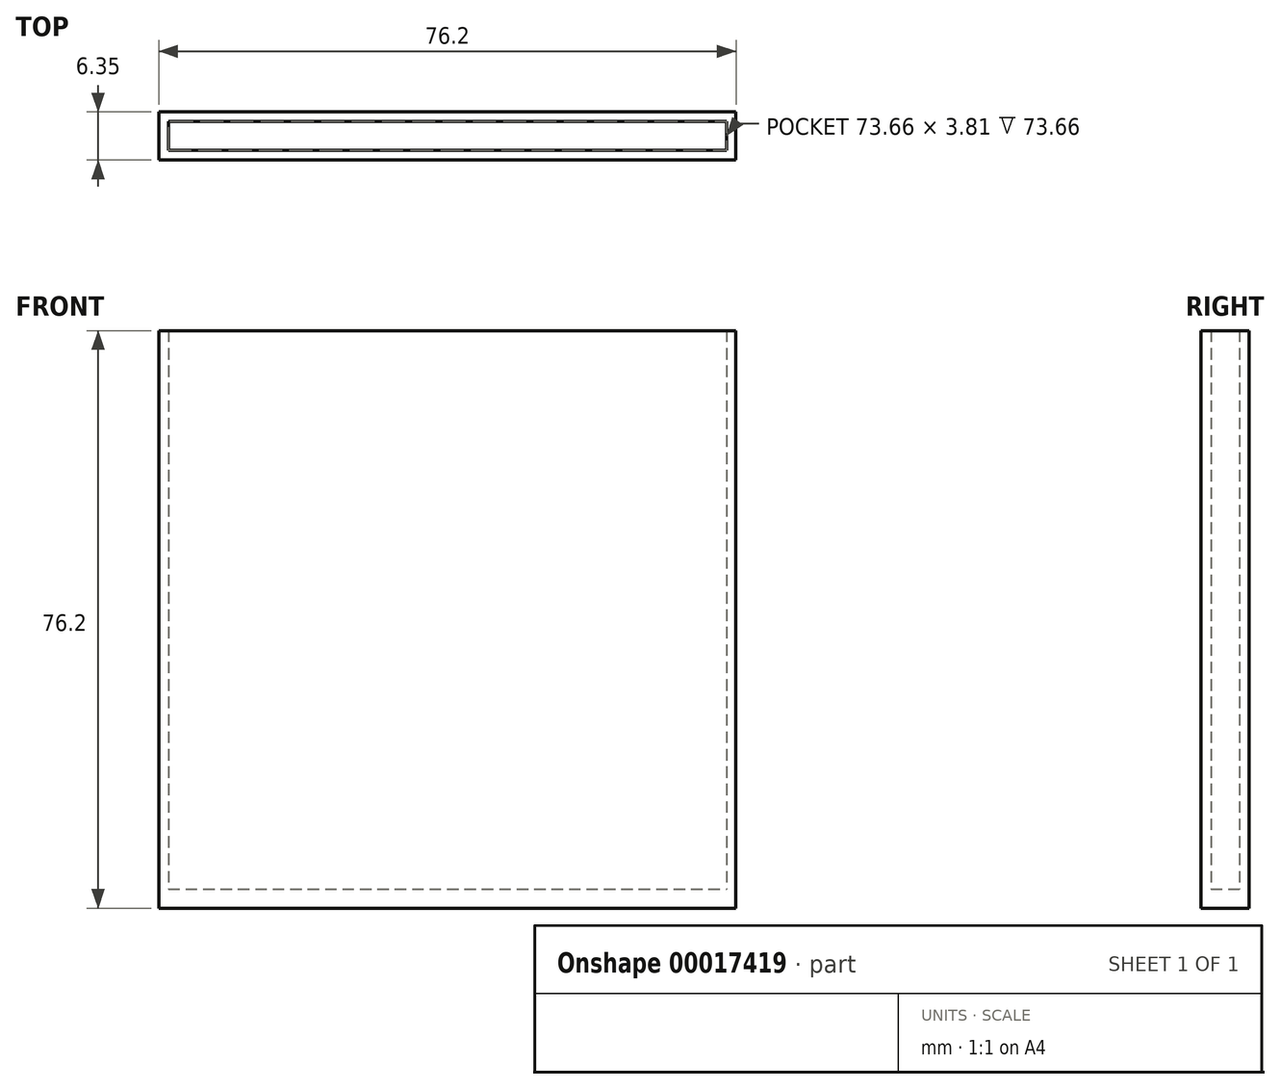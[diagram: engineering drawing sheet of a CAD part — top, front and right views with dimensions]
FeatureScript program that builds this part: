
annotation { "Feature Type Name" : "Feature", "Feature Type Description" : "" }
export const myFeature = defineFeature(function(context is Context, id is Id, definition is map)
    precondition{}
    {
        {
            var Q0;
            Q0=qCreatedBy(makeId("Top.planeOp"),FACE);
            var sketch = newSketch(context, id + "F0", { "sketchPlane" : qUnion([Q0])});
            skLineSegment(sketch, "E0.bottom", {"start": v(-18.72, -3.48) * mm, "end": v(57.48, -3.48) * mm});
            skLineSegment(sketch, "E0.top", {"start": v(-18.72, 2.87) * mm, "end": v(57.48, 2.87) * mm});
            skLineSegment(sketch, "E0.left", {"start": v(-18.72, -3.48) * mm, "end": v(-18.72, 2.87) * mm});
            skLineSegment(sketch, "E0.right", {"start": v(57.48, -3.48) * mm, "end": v(57.48, 2.87) * mm});
            skLineSegment(sketch, "E1.bottom", {"start": v(-17.45, -2.2) * mm, "end": v(56.2, -2.2) * mm});
            skLineSegment(sketch, "E1.top", {"start": v(-17.45, 1.6) * mm, "end": v(56.2, 1.6) * mm});
            skLineSegment(sketch, "E1.left", {"start": v(-17.45, -2.2) * mm, "end": v(-17.45, 1.6) * mm});
            skLineSegment(sketch, "E1.right", {"start": v(56.2, -2.2) * mm, "end": v(56.2, 1.6) * mm});
            skSolve(sketch);
        }
        {
            var Q0;
            Q0=makeQuery(id+"F0.imprint","IMPRINT",FACE,{"disambiguationData":[TD([[makeQuery(id+"F0.imprint","IMPRINT",EDGE,{"derivedFrom":sQuery(id+"F0.wireOp",EDGE,"E0.bottom")}),1.0]])]});
            extrude(context, id + "F1", {"entities" : qUnion([Q0]), "depth" : 76.2 * mm});
        }
        {
            var Q0;
            Q0=makeQuery(id+"F0.imprint","IMPRINT",FACE,{"disambiguationData":[TD([[makeQuery(id+"F0.imprint","IMPRINT",EDGE,{"derivedFrom":sQuery(id+"F0.wireOp",EDGE,"E1.bottom")}),1.0]])]});
            extrude(context, id + "F2", {"entities" : qUnion([Q0]), "operationType" : NewBodyOperationType.ADD, "depth" : 2.54 * mm});
        }
    });
